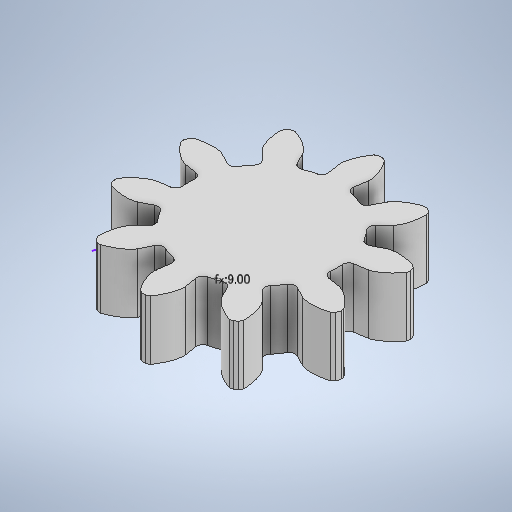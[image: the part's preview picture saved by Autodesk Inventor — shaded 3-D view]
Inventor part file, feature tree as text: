
AUTODESK INVENTOR PART (.ipt)
format: ipt  version: 2025.2 (Build 292293000, 293)  size: 419,328 bytes
history: native  units: mm
features: sketch x3, other x2, extrude x2, fillet x1, chamfer x1, mirror x1, pattern_circular x1
ambient origin geometry x8: Origin, YZ Plane, XZ Plane, XY Plane, X Axis, Y Axis, Z Axis, Center Point
bodies: Body1 (feature_tree)
feature tree (11):
  other  "ソリッド1"
  sketch  "スケッチ2"
  extrude  "押し出し1"  Depth=10.0mm TaperAngle=0.0deg
  extrude  "押し出し2"  Depth=1.570796mm
  fillet  "フィレット1"  Radius=12.0mm
  chamfer  "面取り1"  Distance=3.0mm
  mirror  "ミラー1"
  pattern_circular  "円形状パターン1"  [2 undecoded]
  other  "2D 計算式曲線3"
  sketch  "スケッチ3"
  sketch  "スケッチ4"
note: 2 required parameter values undecoded (feature->parameter linkage not recoverable at this tier; creation-order binding heuristic only, values carry confidence <= 0.55)
